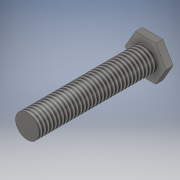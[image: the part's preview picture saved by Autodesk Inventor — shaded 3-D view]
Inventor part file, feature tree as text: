
AUTODESK INVENTOR PART (.ipt)
format: ipt  version: 2018 (Build 220112000, 112)  size: 114,688 bytes
history: native  units: in
note: dims shown in document units (in); Inventor stores cm internally (conversion verified against a paired STEP export)
features: extrude x2, sketch x2, thread x1
ambient origin geometry x8: Origin, YZ Plane, XZ Plane, XY Plane, X Axis, Y Axis, Z Axis, Center Point
bodies: Solid1 (feature_tree)
feature tree (5):
  extrude  "Extrusion1"  Depth=0.15in TaperAngle=0.0deg
  extrude  "Extrusion2"  Depth=2.5in TaperAngle=0.0deg
  thread  "Thread1"  [1 undecoded]
  sketch  "Sketch1"  dims[d0=0.75in d1=0.15in d2=0.0in]
  sketch  "Sketch2"  dims[d3=0.5in d4=2.5in d5=0.0in d6=1.0in d7=1.0in]
note: 1 required parameter value undecoded (feature->parameter linkage not recoverable at this tier; creation-order binding heuristic only, values carry confidence <= 0.55)
